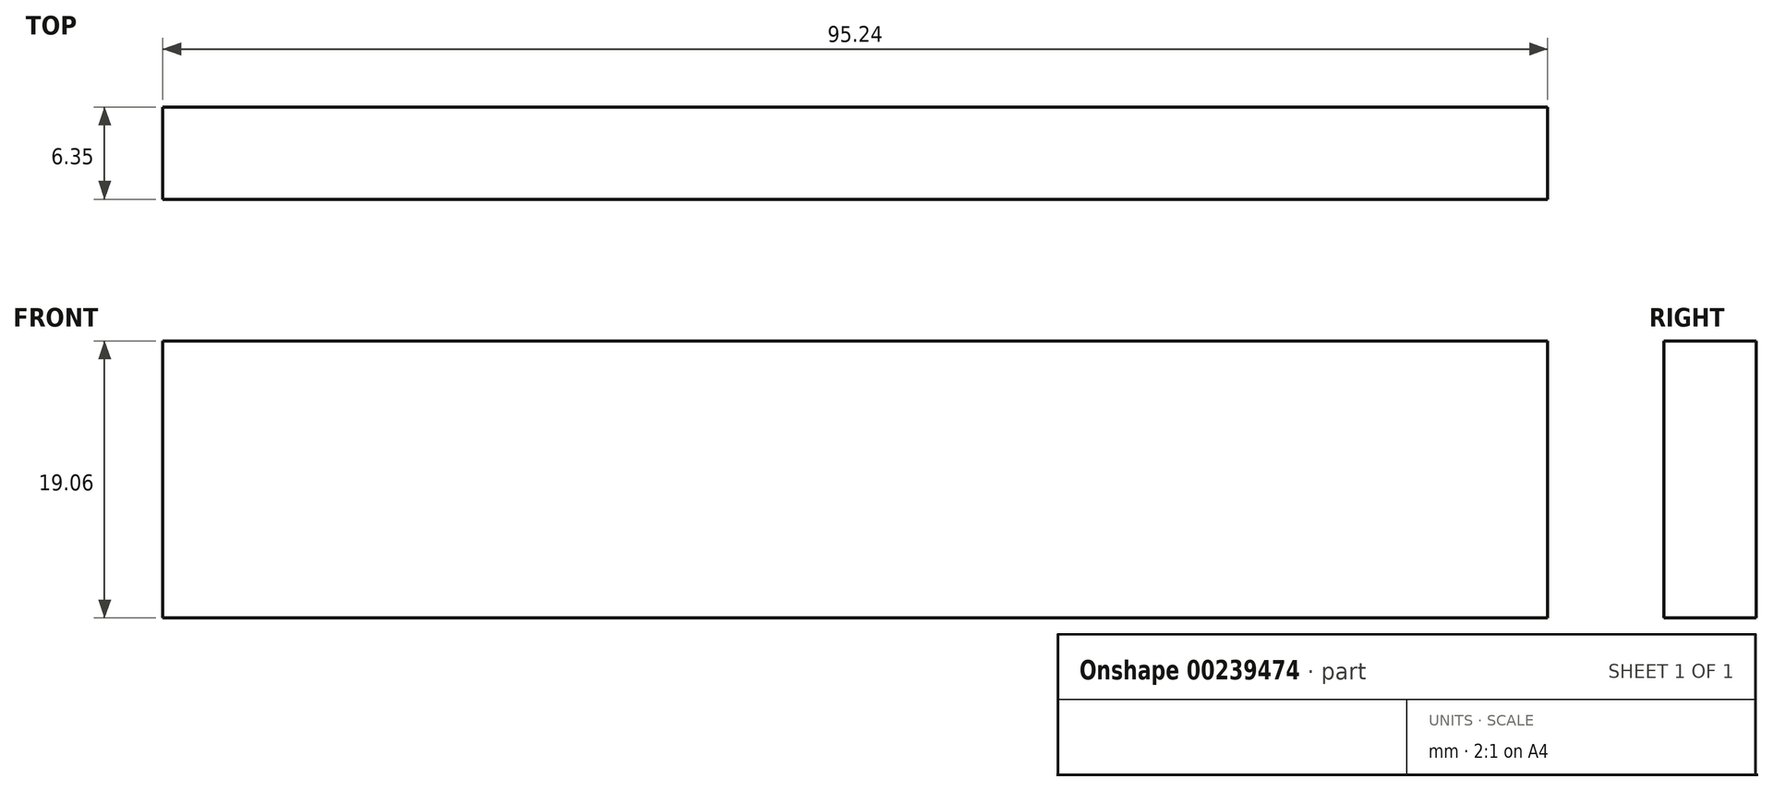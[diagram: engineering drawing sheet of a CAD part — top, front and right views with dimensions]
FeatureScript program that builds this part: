
annotation { "Feature Type Name" : "Feature", "Feature Type Description" : "" }
export const myFeature = defineFeature(function(context is Context, id is Id, definition is map)
    precondition{}
    {
        {
            var Q0;
            Q0=qCreatedBy(makeId("Front.planeOp"),FACE);
            var sketch = newSketch(context, id + "F0", { "sketchPlane" : qUnion([Q0])});
            skLineSegment(sketch, "E0.bottom", {"start": v(-47.63, 9.52) * mm, "end": v(47.63, 9.52) * mm});
            skLineSegment(sketch, "E0.top", {"start": v(-47.63, -9.52) * mm, "end": v(47.63, -9.52) * mm});
            skLineSegment(sketch, "E0.left", {"start": v(-47.62, 9.52) * mm, "end": v(-47.63, -9.52) * mm});
            skLineSegment(sketch, "E0.right", {"start": v(47.63, 9.52) * mm, "end": v(47.63, -9.52) * mm});
            skPoint(sketch, "E0.middle", {"position": v(0, 0) * mm});
            skSolve(sketch);
        }
        {
            var Q0;
            Q0 = qSketchRegion(id + "F0", true);
            extrude(context, id + "F1", {"entities" : qUnion([Q0]), "depth" : 6.35 * mm});
        }
    });
